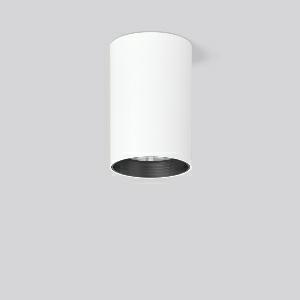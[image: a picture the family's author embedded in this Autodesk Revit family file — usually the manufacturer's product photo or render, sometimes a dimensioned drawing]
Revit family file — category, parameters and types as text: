
# Revit family: heledon_maxi_a_931221_002_76_31b8
name_source: partatom
category: Lighting Fixtures
units: mm (PartAtom-declared; Revit-internal decimal feet)

## family parameters
Cut with Voids When Loaded = No
Host = Face
Light Source = No
Part Type = Normal
Room Calculation Point = No
Round Connector Dimension = Use Diameter
Shared = No

## types (1)
- HELEDON maxi A (1 x LED Modul 930, 2750 lm, 3000)
    Apparent Load = 25 VA
    Approval mark = CE
    CIE Flux Codes = 96 100 100 100 100
    Color Rendering = 90
    Color Temperature = 3000
    Default Elevation = 1800 mm
    Description = Series: HELEDON maxi
Cylindrical surface-mounted downlight. Housing: die-cast aluminium, powder-coated. Internal ceiling frame polycarbonate with bayonet mounting. Black plastic ring and recessed LED to prevent glare from the side. Optical assembly with lens made of plastic (polycarbonate) for the best homogeneous light distribution - can be changed without tools. Best colour rendering index Ra>90. Suitable for Ceiling mounting. Easy installation with a separate ceiling frame with bayonet mounting and plug connection. Driver integrated. Connected via plug-in connector. High quality converter without flickering and stroboscopic effect. The following accessories can be mounted without use of tools: interchangeable lenses, decorative glasses, honeycomb louvre, clear and frosted diffusers, white interchangeable plastic ring. 
Colour: traffic white, matt (RAL 9016)
Diameter: 123 mm
Height: 183 mm
Lamp: LED
Socket: without socket
Colour temperature: 3000K
Colour rendering index (CRI): 92
System power: 25 W
Rated luminous flux: 2750 lm
Luminous efficiency: 110 lm/W
Control gear: Converter, dimmable, DALI
Protection class: I
Type of protection: IP 20
    Height = 183 mm
    Lamp = 1 x LED Modul 930
    Lamp Light Flux = 2750 lm
    Lamp count = 1
    Length = 123 mm
    Lifetime = 50000 h
    Luminous efficacy = 110 lm/W
    Manufacturer = RZB
    ModVariant = No
    Model = 931221.002.76
    Mounting Place = Ceiling
    Mounting Type = Surface mounted
    Number of Poles = 1
    OnlyDefault = Yes
    Power Factor = 1
    Product Name = HELEDON maxi A
    Product group = Surface mounted downlights
    ProductGroupID = 302
    Protection Class = Protection class I
    Protection Degree = IP 20
    RLX_Detail_Level = 1
    RLX_Emergency_Light_Flux = 0 lm
    RLX_Emergency_Type = 0
    RLX_Emergency_Type_DB = No
    RlxData = <blob elided: 99441 chars, md5=aec14742>
    Socket = socket
    Standby Power = 0 W
    System Light Flux = 2750 lm
    System Power = 25 W
    Type Comments = Product without accessories
    Type Image = 931193.002.jpg
    URL = http://relux.com
    VarID = ---
    Voltage = 230 V
    Voltage Range = 220-240 V
    Weight = 0.00 kg
    Width = 0 mm  [stored 0 ft]

note: [stored X ft] marks values corroborated as IEEE doubles in the binary element streams (Revit-internal decimal feet)

## geometry (parser evidence)
native form markers: Blend x4, Sweep x10
no freeform markers — native parametric forms only
